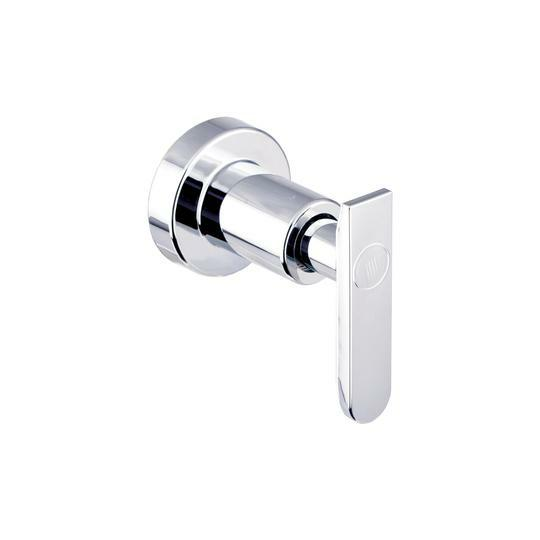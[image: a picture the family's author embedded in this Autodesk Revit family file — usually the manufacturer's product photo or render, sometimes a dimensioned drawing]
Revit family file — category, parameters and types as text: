
# Revit family: 01-1535-211 MEZCLADOR DUCHA 8 SST PIANA
name_source: partatom
category: Aparatos sanitarios
revit_build: Autodesk Revit 2018 (Build: 20170223_1515(x64)
units: mm (PartAtom-declared; Revit-internal decimal feet)

## family parameters
Anfitrión = Cara
Compartido = No
Corte con vacíos al cargar = No
Cota de conector redondo = Diámetro de uso
Número OmniClass = 23.31.11.00
Punto de cálculo de habitación = No
Tipo de pieza = Normal

## types (1)
- 01-1535-211
    Alto = 75 mm
    Ancho = 60 mm  [stored 0.19685 ft]
    Conexión AC = Sí
    Conexión AF = Sí
    Conexión de residuos = No
    Conexión de ventilación = No
    Descripción = Mezclador ducha
    Distancia entre griferias = 203 mm
    Elevación por defecto = 0 mm  [stored 0 ft]
    Fabricante = Gricol
    Imagen de tipo = <Ninguno>
    Link Ficha Tecnica = https://infotecnica.gricol.com
    Metal Acero Inoxidable Cromado = Metal Acero Inoxidable Cromado
    Metal Laton Cromado = Metal Laton Cromado
    Mezclador = Mezclador
    Modelo = 01-1535-211
    Plastico ABS Cromado = Plastico ABS Cromado
    Product Name = MEZCLADOR DUCHA 8 SST PIANA
    Profundidad = 85 mm
    Sepacion entre registro y ducha = 400 mm  [stored 1.31234 ft]
    URL = https://www.gricol.com

note: [stored X ft] marks values corroborated as IEEE doubles in the binary element streams (Revit-internal decimal feet)

## geometry (parser evidence)
native form markers: Blend x2, Sweep x18
no freeform markers — native parametric forms only
